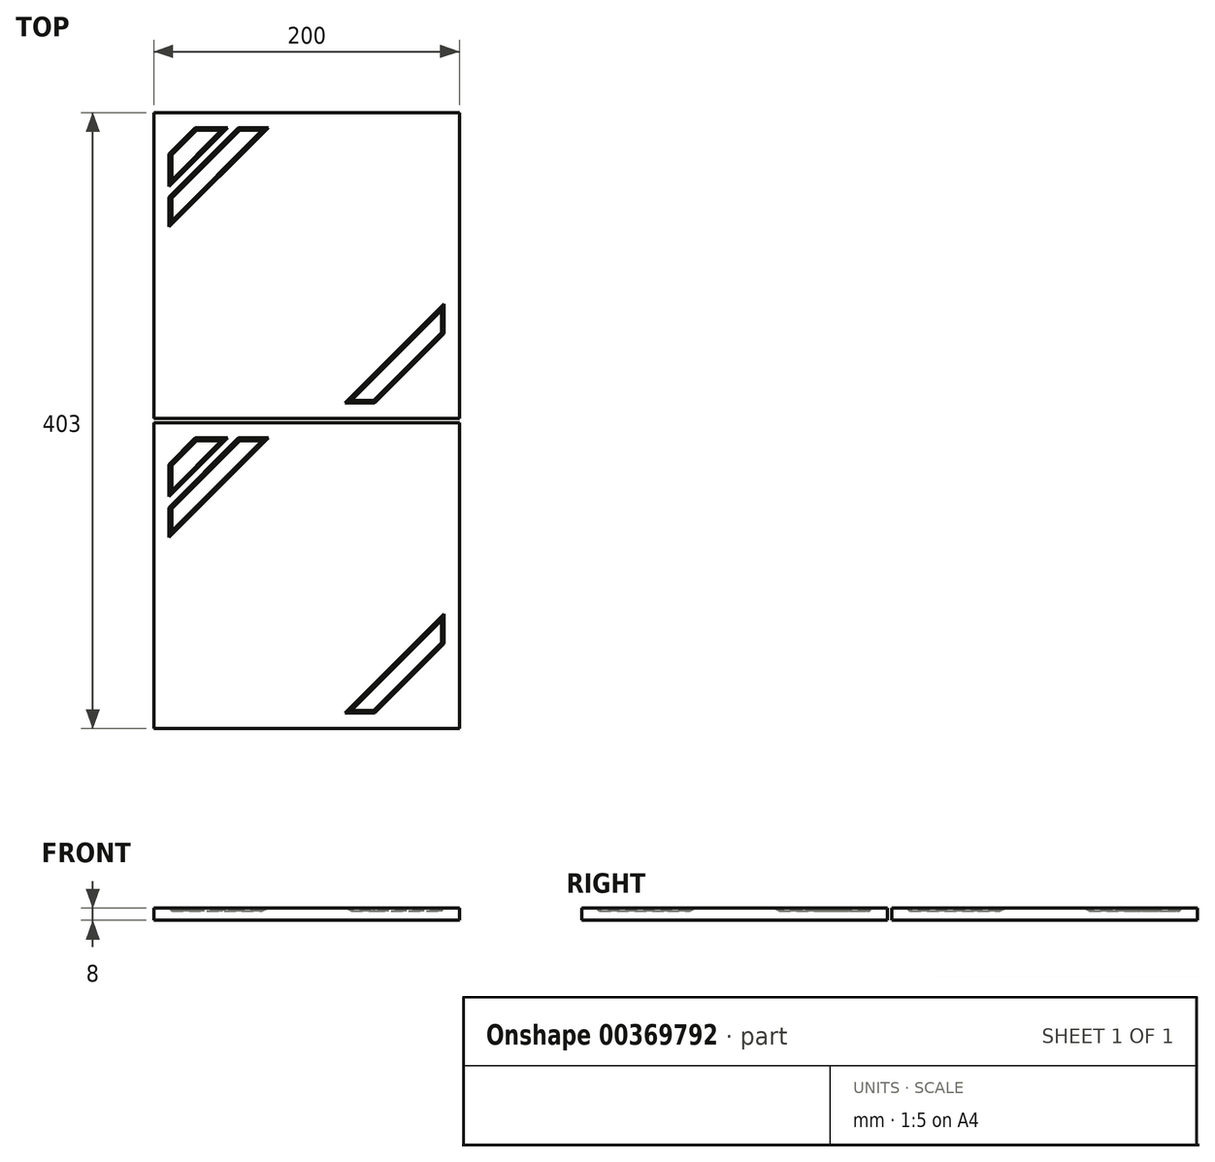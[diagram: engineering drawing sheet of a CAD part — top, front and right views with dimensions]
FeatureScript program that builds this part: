
annotation { "Feature Type Name" : "Feature", "Feature Type Description" : "" }
export const myFeature = defineFeature(function(context is Context, id is Id, definition is map)
    precondition{}
    {
        {
            var Q0;
            Q0=qCreatedBy(makeId("Top.planeOp"),FACE);
            var sketch = newSketch(context, id + "F0", { "sketchPlane" : qUnion([Q0])});
            skLineSegment(sketch, "E0.bottom", {"start": v(100, -100) * mm, "end": v(-100, -100) * mm});
            skLineSegment(sketch, "E0.top", {"start": v(100, 100) * mm, "end": v(-100, 100) * mm});
            skLineSegment(sketch, "E0.left", {"start": v(100, -100) * mm, "end": v(100, 100) * mm});
            skLineSegment(sketch, "E0.right", {"start": v(-100, -100) * mm, "end": v(-100, 100) * mm});
            skPoint(sketch, "E0.middle", {"position": v(0, 0) * mm});
            skLineSegment(sketch, "E1", {"start": v(-90, 44.56) * mm, "end": v(-44.56, 90) * mm});
            skLineSegment(sketch, "E2", {"start": v(-44.56, 90) * mm, "end": v(-25.16, 90) * mm});
            skLineSegment(sketch, "E3", {"start": v(-25.16, 90) * mm, "end": v(-90, 25.16) * mm});
            skLineSegment(sketch, "E4", {"start": v(-90, 25.16) * mm, "end": v(-90, 44.56) * mm});
            skLineSegment(sketch, "E5.0", {"start": v(-90, 51.63) * mm, "end": v(-51.63, 90) * mm});
            skLineSegment(sketch, "E6", {"start": v(-51.63, 90) * mm, "end": v(-72.84, 90) * mm});
            skLineSegment(sketch, "E7", {"start": v(-90, 51.63) * mm, "end": v(-90, 72.84) * mm});
            skLineSegment(sketch, "E8.trimOffspring", {"start": v(-90, 72.84) * mm, "end": v(-72.84, 90) * mm});
            skLineSegment(sketch, "E9", {"start": v(100, 100) * mm, "end": v(-100, -100) * mm, "construction": true});
            skLineSegment(sketch, "E10.MirrorCS", {"start": v(51.63, -90) * mm, "end": v(72.84, -90) * mm});
            skLineSegment(sketch, "E11.MirrorCS", {"start": v(25.16, -90) * mm, "end": v(44.56, -90) * mm});
            skLineSegment(sketch, "E12.MirrorCS", {"start": v(44.56, -90) * mm, "end": v(90, -44.56) * mm});
            skLineSegment(sketch, "E13.MirrorCS", {"start": v(72.84, -90) * mm, "end": v(90, -72.84) * mm});
            skLineSegment(sketch, "E14.MirrorCS", {"start": v(90, -44.56) * mm, "end": v(90, -25.16) * mm});
            skLineSegment(sketch, "E15.MirrorCS", {"start": v(51.63, -90) * mm, "end": v(90, -51.63) * mm});
            skLineSegment(sketch, "E16.MirrorCS", {"start": v(90, -51.63) * mm, "end": v(90, -72.84) * mm});
            skLineSegment(sketch, "E17.MirrorCS", {"start": v(90, -25.16) * mm, "end": v(25.16, -90) * mm});
            skSolve(sketch);
        }
        {
            var Q0;
            Q0=makeQuery(id+"F0.imprint","IMPRINT",FACE,{"disambiguationData":[TD([[makeQuery(id+"F0.imprint","IMPRINT",EDGE,{"derivedFrom":sQuery(id+"F0.wireOp",EDGE,"E0.bottom")}),-1.0]])]});
            var Q1;
            Q1=makeQuery(id+"F0.imprint","IMPRINT",FACE,{"disambiguationData":[TD([[makeQuery(id+"F0.imprint","IMPRINT",EDGE,{"derivedFrom":sQuery(id+"F0.wireOp",EDGE,"kIcSKOVu-Bjrc-ym70-tFiW-ER07qDP8VxE2.bottom")}),-1.0]])]});
            var Q2;
            Q2=makeQuery(id+"F0.imprint","IMPRINT",FACE,{"disambiguationData":[TD([[makeQuery(id+"F0.imprint","IMPRINT",EDGE,{"derivedFrom":sQuery(id+"F0.wireOp",EDGE,"E5.0")}),1.0]])]});
            var Q3;
            Q3=makeQuery(id+"F0.imprint","IMPRINT",FACE,{"disambiguationData":[TD([[makeQuery(id+"F0.imprint","IMPRINT",EDGE,{"derivedFrom":sQuery(id+"F0.wireOp",EDGE,"E1")}),-1.0]])]});
            var Q4;
            Q4=makeQuery(id+"F0.imprint","IMPRINT",FACE,{"disambiguationData":[TD([[makeQuery(id+"F0.imprint","IMPRINT",EDGE,{"derivedFrom":sQuery(id+"F0.wireOp",EDGE,"E11.MirrorCS")}),1.0]])]});
            var Q5;
            Q5=makeQuery(id+"F0.imprint","IMPRINT",FACE,{"disambiguationData":[TD([[makeQuery(id+"F0.imprint","IMPRINT",EDGE,{"derivedFrom":sQuery(id+"F0.wireOp",EDGE,"E10.MirrorCS")}),1.0]])]});
            extrude(context, id + "F1", {"entities" : qUnion([Q0, Q1, Q2, Q3, Q4, Q5]), "depth" : 8 * mm});
        }
        {
            var Q0;
            Q0=makeQuery(id+"F1.opExtrude","CAP_FACE",FACE,{"disambiguationData":[OSD([sQuery(id+"F0.wireOp",EDGE,"E0.bottom"),sQuery(id+"F0.wireOp",EDGE,"E0.top"),sQuery(id+"F0.wireOp",EDGE,"E0.left"),sQuery(id+"F0.wireOp",EDGE,"E0.right")])],"isStart":false});
            var sketch = newSketch(context, id + "F2", { "sketchPlane" : qUnion([Q0])});
            skLineSegment(sketch, "E18.0", {"start": v(-51.63, 90) * mm, "end": v(-72.84, 90) * mm});
            skLineSegment(sketch, "E19.0", {"start": v(-90, 72.84) * mm, "end": v(-72.84, 90) * mm});
            skLineSegment(sketch, "E20.0", {"start": v(-90, 51.63) * mm, "end": v(-90, 72.84) * mm});
            skLineSegment(sketch, "E21.0", {"start": v(-90, 51.63) * mm, "end": v(-51.63, 90) * mm});
            skLineSegment(sketch, "E22.0", {"start": v(-90, 44.56) * mm, "end": v(-44.56, 90) * mm});
            skLineSegment(sketch, "E23.0", {"start": v(-44.56, 90) * mm, "end": v(-25.16, 90) * mm});
            skLineSegment(sketch, "E24.0", {"start": v(-90, 25.16) * mm, "end": v(-90, 44.56) * mm});
            skLineSegment(sketch, "E25.0", {"start": v(-25.16, 90) * mm, "end": v(-90, 25.16) * mm});
            skLineSegment(sketch, "E26.0", {"start": v(90, -25.16) * mm, "end": v(25.16, -90) * mm});
            skLineSegment(sketch, "E26.1", {"start": v(44.56, -90) * mm, "end": v(90, -44.56) * mm});
            skLineSegment(sketch, "E26.2", {"start": v(90, -44.56) * mm, "end": v(90, -25.16) * mm});
            skLineSegment(sketch, "E26.3", {"start": v(25.16, -90) * mm, "end": v(44.56, -90) * mm});
            skLineSegment(sketch, "E26.4", {"start": v(51.63, -90) * mm, "end": v(90, -51.63) * mm});
            skLineSegment(sketch, "E26.5", {"start": v(51.63, -90) * mm, "end": v(72.84, -90) * mm});
            skLineSegment(sketch, "E26.6", {"start": v(72.84, -90) * mm, "end": v(90, -72.84) * mm});
            skLineSegment(sketch, "E26.7", {"start": v(90, -51.63) * mm, "end": v(90, -72.84) * mm});
            skSolve(sketch);
        }
        {
            var Q0;
            Q0=makeQuery(id+"F2.imprint","IMPRINT",FACE,{"disambiguationData":[TD([[makeQuery(id+"F2.imprint","IMPRINT",EDGE,{"derivedFrom":sQuery(id+"F2.wireOp",EDGE,"E18.0")}),1.0]])]});
            var Q1;
            Q1=makeQuery(id+"F2.imprint","IMPRINT",FACE,{"disambiguationData":[TD([[makeQuery(id+"F2.imprint","IMPRINT",EDGE,{"derivedFrom":sQuery(id+"F2.wireOp",EDGE,"E22.0")}),-1.0]])]});
            var Q2;
            Q2=makeQuery(id+"F2.imprint","IMPRINT",FACE,{"disambiguationData":[TD([[makeQuery(id+"F2.imprint","IMPRINT",EDGE,{"derivedFrom":sQuery(id+"F2.wireOp",EDGE,"E26.0")}),1.0]])]});
            extrude(context, id + "F3", {"entities" : qUnion([Q0, Q1, Q2]), "operationType" : NewBodyOperationType.REMOVE, "oppositeDirection" : true, "depth" : 2 * mm, "hasDraft" : true, "draftAngle" : 40 * degree, "draftPullDirection" : true});
        }
        {
            var Q0;
            Q0=makeQuery(id+"F1.opExtrude","SWEPT_BODY",BODY,{"disambiguationData":[OSD([sQuery(id+"F0.wireOp",EDGE,"E0.bottom"),sQuery(id+"F0.wireOp",EDGE,"E0.top"),sQuery(id+"F0.wireOp",EDGE,"E0.left"),sQuery(id+"F0.wireOp",EDGE,"E0.right")])]});
            transform(context, id + "F4", {"entities" : qUnion([Q0]), "transformType" : TransformType.TRANSLATION_3D, "dx" : 0 * mm, "dy" : 203 * mm, "dz" : 0 * mm, "makeCopy" : true});
        }
    });
